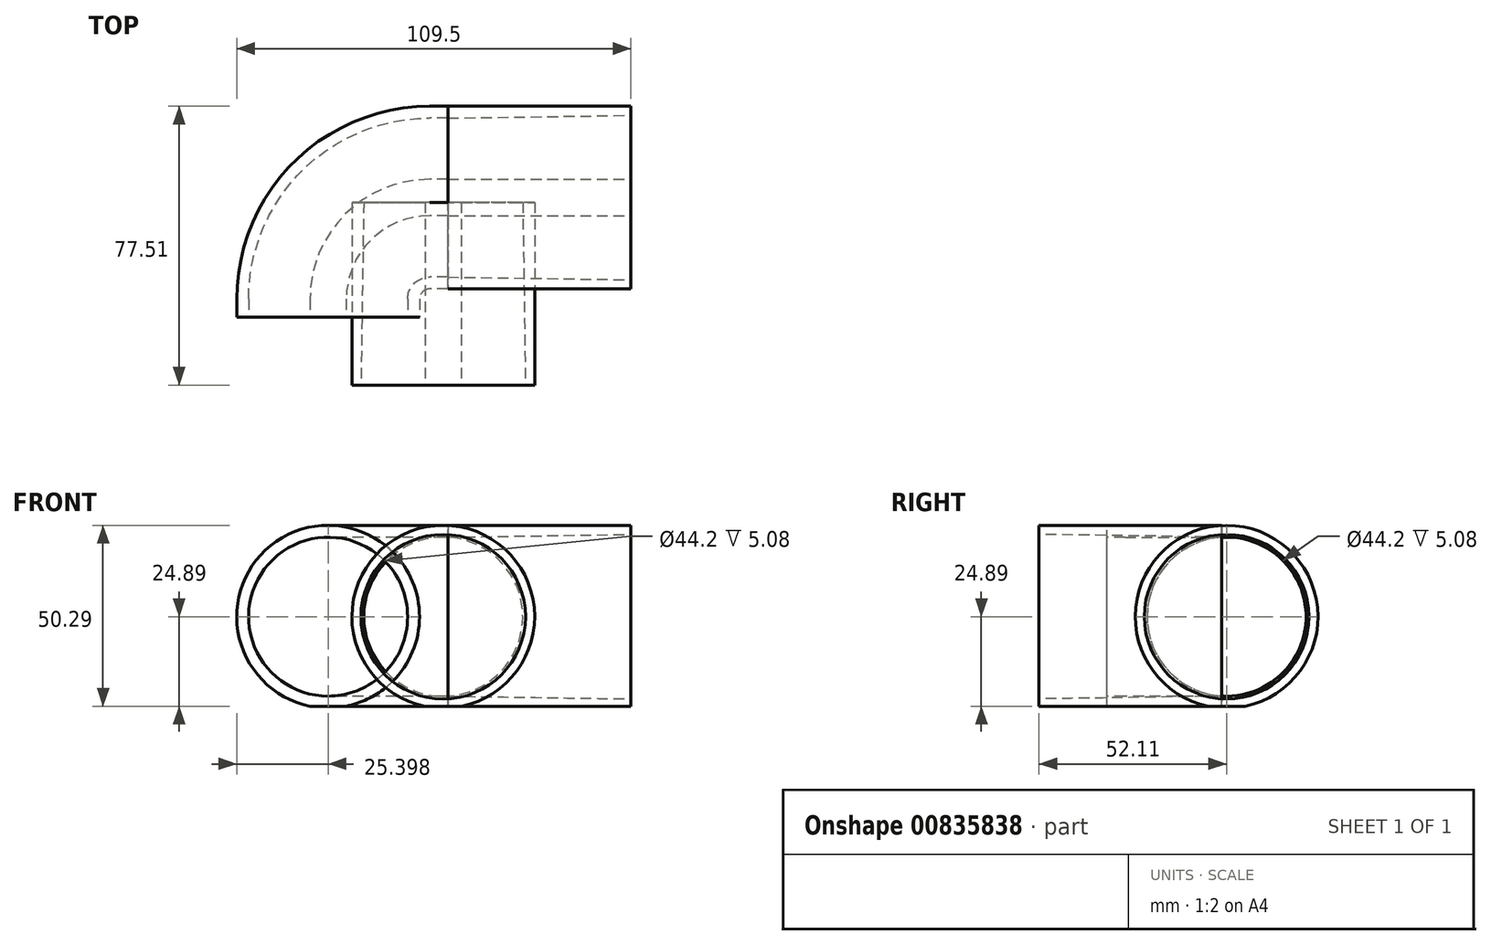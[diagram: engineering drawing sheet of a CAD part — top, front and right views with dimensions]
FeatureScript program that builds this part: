
annotation { "Feature Type Name" : "Feature", "Feature Type Description" : "" }
export const myFeature = defineFeature(function(context is Context, id is Id, definition is map)
    precondition{}
    {
        {
            assignVariable(context, id + "F0", {"name" : "OD", "anyValue" : 2});
        }
        {
            var Q0;
            Q0=qCreatedBy(makeId("Front.planeOp"),FACE);
            var sketch = newSketch(context, id + "F1", { "sketchPlane" : qUnion([Q0])});
            skLineSegment(sketch, "E0", {"start": v(0, 0) * mm, "end": v(-103.9, 0) * mm, "construction": true});
            skLineSegment(sketch, "E1", {"start": v(0, 25.4) * mm, "end": v(0, 22.1) * mm});
            skLineSegment(sketch, "E2", {"start": v(0, 22.1) * mm, "end": v(50.8, 22.86) * mm});
            skLineSegment(sketch, "E3", {"start": v(50.8, 22.86) * mm, "end": v(50.8, 25.4) * mm});
            skLineSegment(sketch, "E4", {"start": v(50.8, 25.4) * mm, "end": v(0, 25.4) * mm});
            skPoint(sketch, "E5", {"position": v(25.4, 22.48) * mm});
            skSolve(sketch);
        }
        {
            var Q0;
            Q0=qSketchRegion(id+"F1",true);
            var Q1;
            Q1=sQuery(id+"F1.wireOp",EDGE,"E0");
            revolve(context, id + "F2", {"surfaceOperationType" : NewSurfaceOperationType.NEW, "entities" : qUnion([Q0]), "axis" : qUnion([Q1]), "revolveType" : RevolveType.FULL});
        }
        {
            var Q0;
            Q0=qCreatedBy(makeId("Right.planeOp"),FACE);
            cPlane(context, id + "F3", {"entities" : qUnion([Q0]), "cplaneType" : CPlaneType.OFFSET, "offset" : ((getVariable(context, 'OD') / 1.8) + (getVariable(context, 'OD') / 10)) * mm, "oppositeDirection" : true, "width" : 152.4 * mm, "height" : 152.4 * mm});
        }
        {
            var Q0;
            Q0=qCreatedBy(id+"F3.planeOp",FACE);
            var sketch = newSketch(context, id + "F4", { "sketchPlane" : qUnion([Q0])});
            skLineSegment(sketch, "E6", {"start": v(0, 0) * mm, "end": v(0, 10.77) * mm, "construction": true});
            skSolve(sketch);
        }
        {
            var Q0;
            Q0=makeQuery(id+"F2.opRevolve","SWEPT_BODY",BODY,{"disambiguationData":[OSD([sQuery(id+"F1.wireOp",EDGE,"E1"),sQuery(id+"F1.wireOp",EDGE,"E2"),sQuery(id+"F1.wireOp",EDGE,"E3"),sQuery(id+"F1.wireOp",EDGE,"E4")])]});
            var Q1;
            Q1=sQuery(id+"F4.wireOp",EDGE,"E6");
            circularPattern(context, id + "F5", {"entities" : qUnion([Q0]), "axis" : qUnion([Q1]), "angle" : 90 * degree, "instanceCount" : 2, "oppositeDirection" : true, "equalSpace" : true});
        }
        {
            var Q0;
            Q0=qCreatedBy(makeId("Top.planeOp"),FACE);
            var sketch = newSketch(context, id + "F6", { "sketchPlane" : qUnion([Q0])});
            skLineSegment(sketch, "E7", {"start": v(0, 0) * mm, "end": v(-5.08, 0) * mm});
            skLineSegment(sketch, "E8", {"start": v(-33.3, -28.22) * mm, "end": v(-33.3, -33.3) * mm});
            skPoint(sketch, "E9.visualSharp", {"position": v(-33.3, 0) * mm});
            skArc(sketch, "E9.filletArc", {"start": v(-5.08, 0) * mm, "mid": v(-25.04, -8.27) * mm, "end": v(-33.3, -28.22) * mm});
            skSolve(sketch);
        }
        {
            var Q0;
            Q0=makeQuery(id+"F2.opRevolve","SWEPT_FACE",FACE,{"disambiguationData":[OSD([sQuery(id+"F1.wireOp",EDGE,"E1")])]});
            var Q1;
            Q1 = qConstructionFilter(qBodyType(qCreatedBy(id + "F6" ,EDGE), BodyType.WIRE), ConstructionObject.NO);
            sweep(context, id + "F7", {"profiles" : qUnion([Q0]), "path" : qUnion([Q1])});
        }
        {
            var Q0;
            Q0=qCreatedBy(makeId("Right.planeOp"),FACE);
            var sketch = newSketch(context, id + "F8", { "sketchPlane" : qUnion([Q0])});
            skLineSegment(sketch, "E10.bottom", {"start": v(-101.6, -24.9) * mm, "end": v(25.4, -24.9) * mm});
            skLineSegment(sketch, "E10.top", {"start": v(-101.6, -25.4) * mm, "end": v(25.4, -25.4) * mm});
            skLineSegment(sketch, "E10.left", {"start": v(-101.6, -25.4) * mm, "end": v(-101.6, -24.9) * mm});
            skLineSegment(sketch, "E10.right", {"start": v(25.4, -25.4) * mm, "end": v(25.4, -24.9) * mm});
            skSolve(sketch);
        }
        {
            var Q0;
            Q0 = qSketchRegion(id + "F8", true);
            extrude(context, id + "F9", {"entities" : qUnion([Q0]), "operationType" : NewBodyOperationType.REMOVE, "endBound" : BoundingType.THROUGH_ALL, "oppositeDirection" : true, "depth" : 25.4 * mm, "offsetDistance" : 25.4 * mm, "hasSecondDirection" : true, "secondDirectionBound" : BoundingType.THROUGH_ALL, "secondDirectionOppositeDirection" : false, "secondDirectionDepth" : 25.4 * mm});
        }
    });
